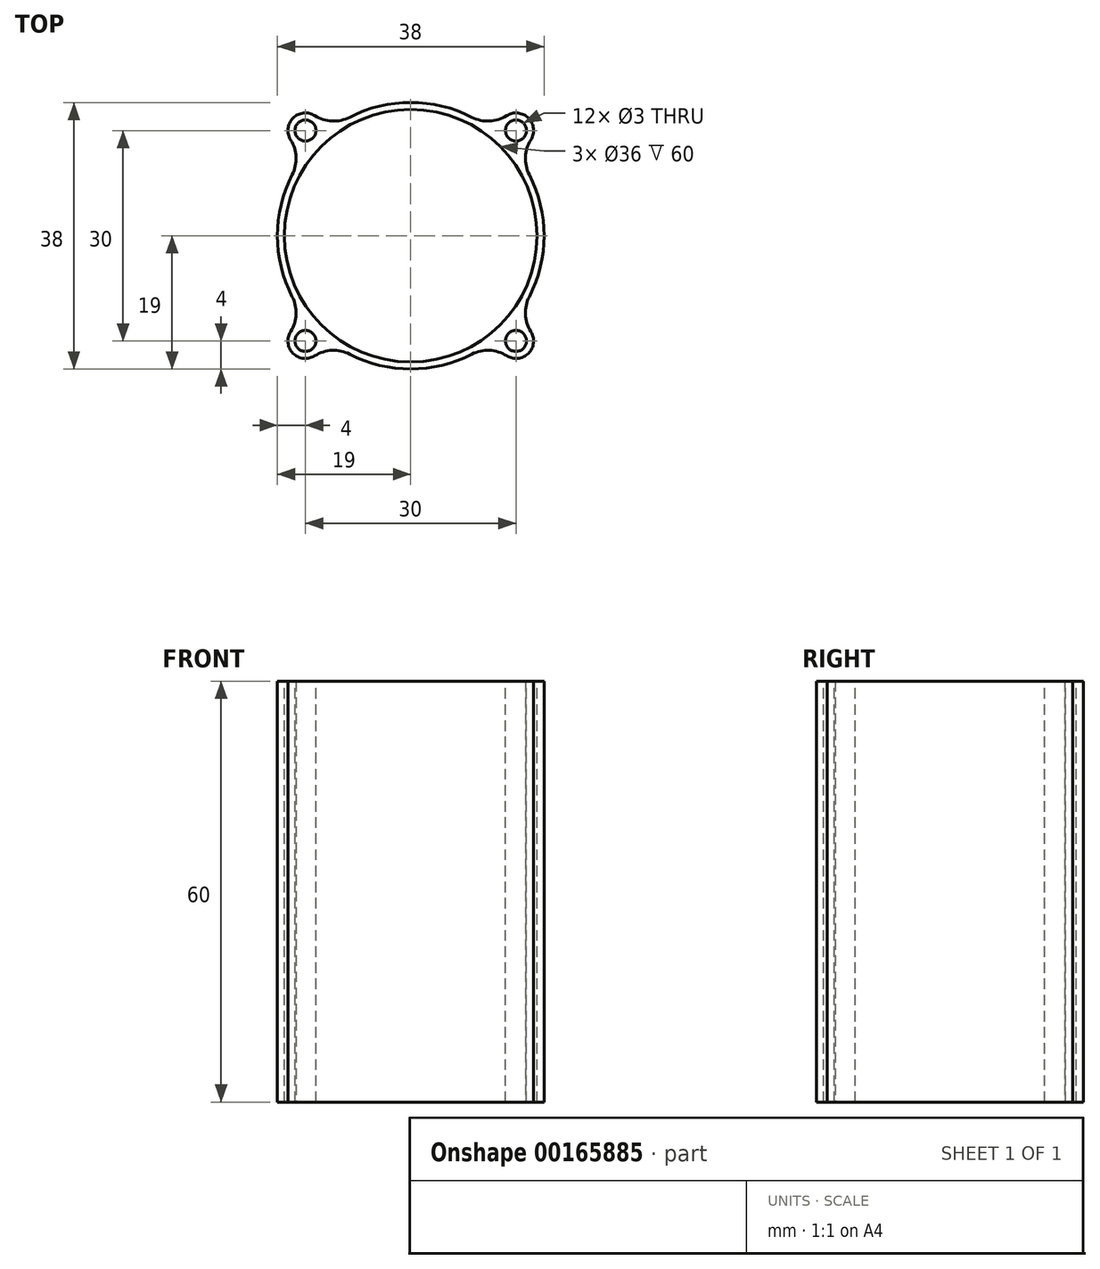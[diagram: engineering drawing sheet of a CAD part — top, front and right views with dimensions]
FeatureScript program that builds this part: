
annotation { "Feature Type Name" : "Feature", "Feature Type Description" : "" }
export const myFeature = defineFeature(function(context is Context, id is Id, definition is map)
    precondition{}
    {
        {
            var Q0;
            Q0=qCreatedBy(makeId("Top.planeOp"),FACE);
            var sketch = newSketch(context, id + "F0", { "sketchPlane" : qUnion([Q0])});
            skCircle(sketch, "E0", {"center": v(0, 0) * mm, "radius": 18 * mm});
            skCircle(sketch, "E1", {"center": v(0, 0) * mm, "radius": 19 * mm});
            skCircle(sketch, "E2", {"center": v(-15, 15) * mm, "radius": 1.5 * mm});
            skCircle(sketch, "E3", {"center": v(-15, 15) * mm, "radius": 2.5 * mm});
            skCircle(sketch, "E4.1.0", {"center": v(-15, -15) * mm, "radius": 2.5 * mm});
            skCircle(sketch, "E4.1.1", {"center": v(-15, -15) * mm, "radius": 1.5 * mm});
            skCircle(sketch, "E4.2.0", {"center": v(15, -15) * mm, "radius": 2.5 * mm});
            skCircle(sketch, "E4.2.1", {"center": v(15, -15) * mm, "radius": 1.5 * mm});
            skCircle(sketch, "E4.3.0", {"center": v(15, 15) * mm, "radius": 2.5 * mm});
            skCircle(sketch, "E4.3.1", {"center": v(15, 15) * mm, "radius": 1.5 * mm});
            skSolve(sketch);
        }
        {
            var Q0;
            Q0=makeQuery(id+"F0.imprint","IMPRINT",FACE,{"disambiguationData":[TD([[makeQuery(id+"F0.imprint","IMPRINT",EDGE,{"derivedFrom":sQuery(id+"F0.wireOp",EDGE,"E2")}),-1.0]])]});
            var Q1;
            {var subQ0=sQuery(id+"F0.wireOp",EDGE,"E4.3.0");var subQ1=sQuery(id+"F0.wireOp",EDGE,"E1");var subQ2=makeQuery(id+"F0.imprint","INTERSECT",VERTEX,{"disambiguationData":[OD(0.0)],"derivedFrom":[subQ1,subQ0]});Q1=makeQuery(id+"F0.imprint","IMPRINT",FACE,{"disambiguationData":[TD([[makeQuery(id+"F0.imprint","IMPRINT",EDGE,{"disambiguationData":[TD([[subQ2,1.0]])],"derivedFrom":subQ1}),1.0]])]});}
            var Q2;
            Q2=makeQuery(id+"F0.imprint","IMPRINT",FACE,{"disambiguationData":[TD([[makeQuery(id+"F0.imprint","IMPRINT",EDGE,{"derivedFrom":sQuery(id+"F0.wireOp",EDGE,"E4.3.1")}),-1.0]])]});
            var Q3;
            {var subQ0=sQuery(id+"F0.wireOp",EDGE,"E4.2.0");var subQ1=sQuery(id+"F0.wireOp",EDGE,"E1");var subQ2=makeQuery(id+"F0.imprint","INTERSECT",VERTEX,{"disambiguationData":[OD(0.0)],"derivedFrom":[subQ1,subQ0]});Q3=makeQuery(id+"F0.imprint","IMPRINT",FACE,{"disambiguationData":[TD([[makeQuery(id+"F0.imprint","IMPRINT",EDGE,{"disambiguationData":[TD([[subQ2,-1.0]])],"derivedFrom":subQ1}),1.0]])]});}
            var Q4;
            Q4=makeQuery(id+"F0.imprint","IMPRINT",FACE,{"disambiguationData":[TD([[makeQuery(id+"F0.imprint","IMPRINT",EDGE,{"derivedFrom":sQuery(id+"F0.wireOp",EDGE,"E4.2.1")}),-1.0]])]});
            var Q5;
            {var subQ0=sQuery(id+"F0.wireOp",EDGE,"E4.1.0");var subQ1=sQuery(id+"F0.wireOp",EDGE,"E1");var subQ2=makeQuery(id+"F0.imprint","INTERSECT",VERTEX,{"disambiguationData":[OD(0.0)],"derivedFrom":[subQ1,subQ0]});Q5=makeQuery(id+"F0.imprint","IMPRINT",FACE,{"disambiguationData":[TD([[makeQuery(id+"F0.imprint","IMPRINT",EDGE,{"disambiguationData":[TD([[subQ2,-1.0]])],"derivedFrom":subQ1}),1.0]])]});}
            var Q6;
            Q6=makeQuery(id+"F0.imprint","IMPRINT",FACE,{"disambiguationData":[TD([[makeQuery(id+"F0.imprint","IMPRINT",EDGE,{"derivedFrom":sQuery(id+"F0.wireOp",EDGE,"E4.1.1")}),-1.0]])]});
            var Q7;
            Q7=makeQuery(id+"F0.imprint","IMPRINT",FACE,{"disambiguationData":[TD([[makeQuery(id+"F0.imprint","IMPRINT",EDGE,{"derivedFrom":sQuery(id+"F0.wireOp",EDGE,"E0")}),-1.0]])]});
            var Q8;
            {var subQ0=sQuery(id+"F0.wireOp",EDGE,"E3");var subQ1=sQuery(id+"F0.wireOp",EDGE,"E1");var subQ2=makeQuery(id+"F0.imprint","INTERSECT",VERTEX,{"disambiguationData":[OD(0.0)],"derivedFrom":[subQ1,subQ0]});Q8=makeQuery(id+"F0.imprint","IMPRINT",FACE,{"disambiguationData":[TD([[makeQuery(id+"F0.imprint","IMPRINT",EDGE,{"disambiguationData":[TD([[subQ2,-1.0]])],"derivedFrom":subQ1}),1.0]])]});}
            extrude(context, id + "F1", {"entities" : qUnion([Q0, Q1, Q2, Q3, Q4, Q5, Q6, Q7, Q8]), "oppositeDirection" : true, "depth" : 60 * mm});
        }
        {
            var Q0;
            {var subQ0=sQuery(id+"F0.wireOp",EDGE,"E3");var subQ1=sQuery(id+"F0.wireOp",EDGE,"E1");Q0=makeQuery(id+"F1.opExtrude","SWEPT_EDGE",EDGE,{"disambiguationData":[OSD([subQ1,subQ0]),TDD([makeQuery(id+"F0.imprint","INTERSECT",VERTEX,{"disambiguationData":[OD(1.0)],"derivedFrom":[subQ1,subQ0]})])]});}
            var Q1;
            {var subQ0=sQuery(id+"F0.wireOp",EDGE,"E4.1.0");var subQ1=sQuery(id+"F0.wireOp",EDGE,"E1");Q1=makeQuery(id+"F1.opExtrude","SWEPT_EDGE",EDGE,{"disambiguationData":[OSD([subQ1,subQ0]),TDD([makeQuery(id+"F0.imprint","INTERSECT",VERTEX,{"disambiguationData":[OD(0.0)],"derivedFrom":[subQ1,subQ0]})])]});}
            var Q2;
            {var subQ0=sQuery(id+"F0.wireOp",EDGE,"E4.3.0");var subQ1=sQuery(id+"F0.wireOp",EDGE,"E1");Q2=makeQuery(id+"F1.opExtrude","SWEPT_EDGE",EDGE,{"disambiguationData":[OSD([subQ1,subQ0]),TDD([makeQuery(id+"F0.imprint","INTERSECT",VERTEX,{"disambiguationData":[OD(0.0)],"derivedFrom":[subQ1,subQ0]})])]});}
            var Q3;
            {var subQ0=sQuery(id+"F0.wireOp",EDGE,"E3");var subQ1=sQuery(id+"F0.wireOp",EDGE,"E1");Q3=makeQuery(id+"F1.opExtrude","SWEPT_EDGE",EDGE,{"disambiguationData":[OSD([subQ1,subQ0]),TDD([makeQuery(id+"F0.imprint","INTERSECT",VERTEX,{"disambiguationData":[OD(0.0)],"derivedFrom":[subQ1,subQ0]})])]});}
            var Q4;
            {var subQ0=sQuery(id+"F0.wireOp",EDGE,"E4.3.0");var subQ1=sQuery(id+"F0.wireOp",EDGE,"E1");Q4=makeQuery(id+"F1.opExtrude","SWEPT_EDGE",EDGE,{"disambiguationData":[OSD([subQ1,subQ0]),TDD([makeQuery(id+"F0.imprint","INTERSECT",VERTEX,{"disambiguationData":[OD(1.0)],"derivedFrom":[subQ1,subQ0]})])]});}
            var Q5;
            {var subQ0=sQuery(id+"F0.wireOp",EDGE,"E4.2.0");var subQ1=sQuery(id+"F0.wireOp",EDGE,"E1");Q5=makeQuery(id+"F1.opExtrude","SWEPT_EDGE",EDGE,{"disambiguationData":[OSD([subQ1,subQ0]),TDD([makeQuery(id+"F0.imprint","INTERSECT",VERTEX,{"disambiguationData":[OD(1.0)],"derivedFrom":[subQ1,subQ0]})])]});}
            var Q6;
            {var subQ0=sQuery(id+"F0.wireOp",EDGE,"E4.2.0");var subQ1=sQuery(id+"F0.wireOp",EDGE,"E1");Q6=makeQuery(id+"F1.opExtrude","SWEPT_EDGE",EDGE,{"disambiguationData":[OSD([subQ1,subQ0]),TDD([makeQuery(id+"F0.imprint","INTERSECT",VERTEX,{"disambiguationData":[OD(0.0)],"derivedFrom":[subQ1,subQ0]})])]});}
            var Q7;
            {var subQ0=sQuery(id+"F0.wireOp",EDGE,"E4.1.0");var subQ1=sQuery(id+"F0.wireOp",EDGE,"E1");Q7=makeQuery(id+"F1.opExtrude","SWEPT_EDGE",EDGE,{"disambiguationData":[OSD([subQ1,subQ0]),TDD([makeQuery(id+"F0.imprint","INTERSECT",VERTEX,{"disambiguationData":[OD(1.0)],"derivedFrom":[subQ1,subQ0]})])]});}
            fillet(context, id + "F2", {"entities" : qUnion([Q0, Q1, Q2, Q3, Q4, Q5, Q6, Q7]), "radius" : 5 * mm, "tangentPropagation" : true, "allowEdgeOverflow" : false});
        }
    });
